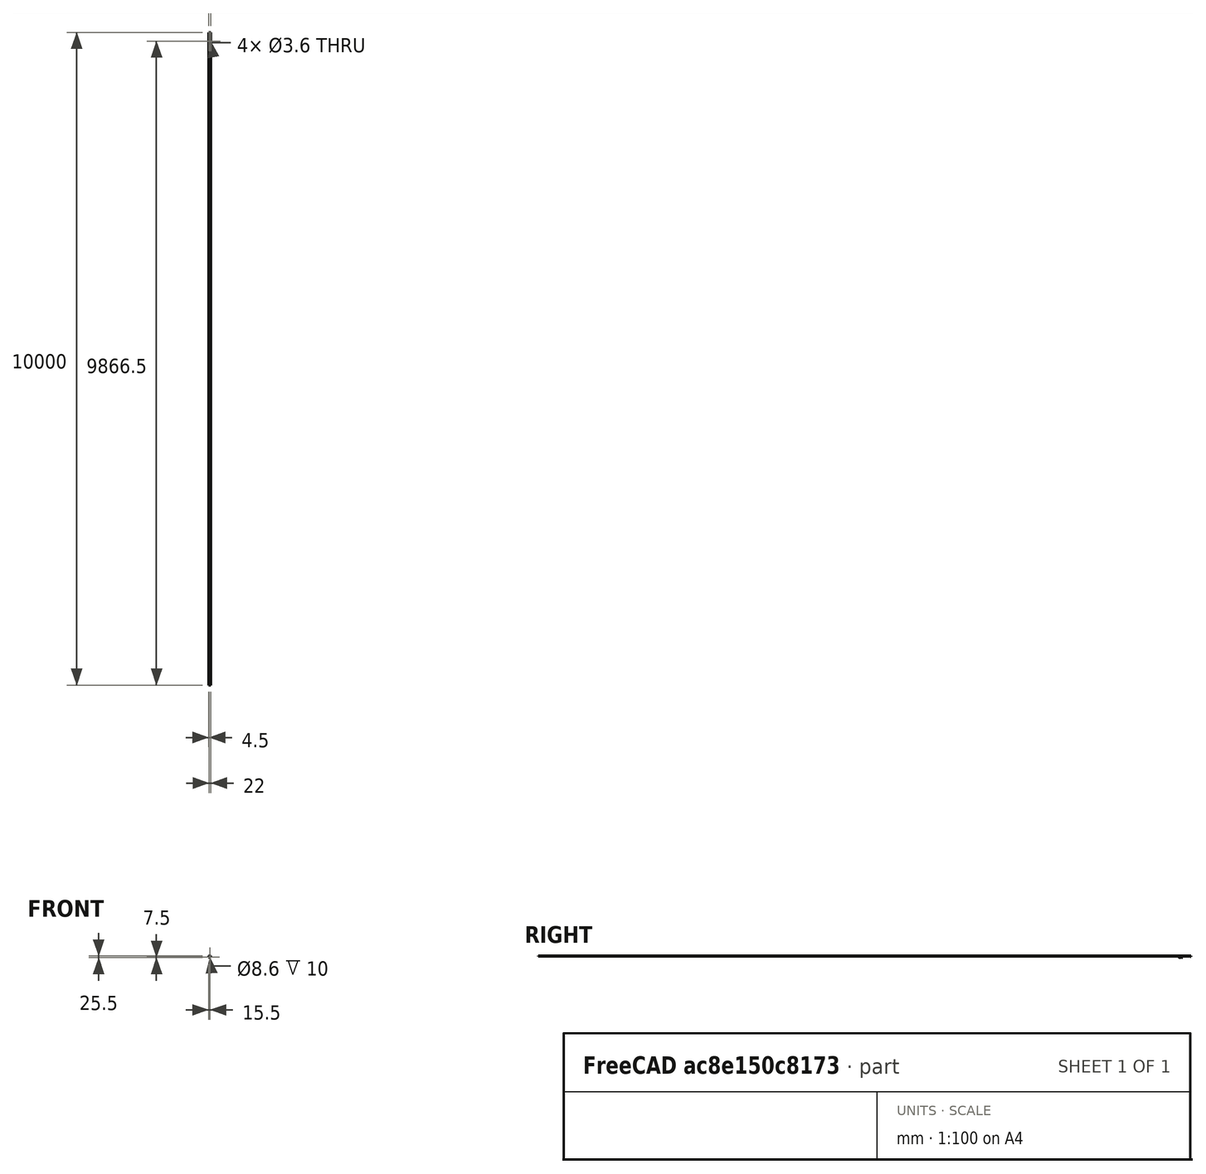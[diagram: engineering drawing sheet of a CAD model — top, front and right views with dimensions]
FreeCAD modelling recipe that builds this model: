
FCSTD DOCUMENT  (FreeCAD 0.15R4671 (Git))
Label: TopRodHolder
License: All rights reserved
LicenseURL: http://en.wikipedia.org/wiki/All_rights_reserved
objects: Sketcher::SketchObject×4, Mesh::Feature×3, PartDesign::Pocket×3, PartDesign::Fillet×2, Part::Feature×1, PartDesign::Pad×1
note: 15 computed .brp shape members not serialized (recipe doc carries the construction recipe); baked Part::Feature solids carry a one-line shape summary decoded from their .brp

FEATURE [Sketcher::SketchObject] Sketch
  Placement = pos=(0,0,0) rot=(1,0,0;3.14159rad)
  sketch-geometry (6):
    g0: LineSegment StartX=51 StartY=69.5 StartZ=0 EndX=21 EndY=69.5 EndZ=0
    g1: LineSegment StartX=21 StartY=69.5 StartZ=0 EndX=21 EndY=58.5 EndZ=0
    g2: LineSegment StartX=21 StartY=58.5 StartZ=0 EndX=51 EndY=58.5 EndZ=0
    g3: LineSegment StartX=51 StartY=58.5 StartZ=0 EndX=51 EndY=69.5 EndZ=0
    g4: Circle CenterX=47 CenterY=64 CenterZ=0 NormalX=0 NormalY=0 NormalZ=1 Radius=1.8
    g5: Circle CenterX=25 CenterY=64 CenterZ=0 NormalX=0 NormalY=0 NormalZ=1 Radius=1.8
  constraints (18):
    c: Coincident(g0,g1)
    c: Coincident(g1,g2)
    c: Coincident(g2,g3)
    c: Coincident(g3,g0)
    c: Horizontal(g0)
    c: Horizontal(g2)
    c: Vertical(g1)
    c: Vertical(g3)
    c: DistanceY(g0,g1) = -11
    c: DistanceX(g0,g0) = 30
    c: DistanceX(g1) = 21
    c: DistanceY(g1) = 58.5
    c: Radius(g4) = 1.8
    c: Radius(g5) = 1.8
    c: DistanceX(g5,g4) = 22
    c: DistanceY(g5,g4) = 0
    c: DistanceX(g5,g1) = -4
    c: DistanceY(g5,g1) = -5.5
FEATURE [Part::Feature] LM8UU_8mm_Linear_Bearing
  Placement = pos=(36,-114.5,-5.5) rot=(0,0,1;1.5708rad)
  shape: bbox 15 x 24 x 15 mm, 34 faces (baked)
FEATURE [Mesh::Feature] _mmRod_x100mm  label="8mmRod_x100mm"
  Placement = pos=(36,-160.5,-5.5) rot=(0,0,1;3.14159rad)
FEATURE [PartDesign::Pad] Pad
  Length = 11.5
  Length2 = 100
  Placement = pos=(0,0,0) rot=(1,0,0;3.14159rad)
  Sketch = -> Sketch
  Type = 0
FEATURE [Sketcher::SketchObject] Sketch001
  Placement = pos=(0,-69.5,0) rot=(0,0.707107,-0.707107;3.14159rad)
  Support = -> Pad [Face1]
  sketch-geometry (6):
    g0: ArcOfCircle CenterX=-36 CenterY=5.5 CenterZ=0 NormalX=0 NormalY=0 NormalZ=1 Radius=6 StartAngle=0 EndAngle=3.14159
    g1: LineSegment StartX=-30 StartY=5.5 StartZ=0 EndX=-20.5 EndY=5.5 EndZ=0
    g2: LineSegment StartX=-20.5 StartY=5.5 StartZ=0 EndX=-20.5 EndY=12.5 EndZ=0
    g3: LineSegment StartX=-20.5 StartY=12.5 StartZ=0 EndX=-51.5 EndY=12.5 EndZ=0
    g4: LineSegment StartX=-51.5 StartY=12.5 StartZ=0 EndX=-51.5 EndY=5.5 EndZ=0
    g5: LineSegment StartX=-51.5 StartY=5.5 StartZ=0 EndX=-42 EndY=5.5 EndZ=0
  constraints (6):
    c: Coincident(g1,g2)
    c: Coincident(g2,g3)
    c: Coincident(g3,g4)
    c: Coincident(g4,g5)
    c: Coincident(g0,g5)
    c: Coincident(g0,g1)
FEATURE [PartDesign::Pocket] Pocket
  Length = 5
  Placement = pos=(0,0,0) rot=(1,0,0;3.14159rad)
  Sketch = -> Sketch001
  Type = 1
FEATURE [Mesh::Feature] HexNutStyle1_M  label="HexNutStyle1_M3"
  Placement = pos=(39.2,-42,-122) rot=(0,0,1;0rad)
FEATURE [Mesh::Feature] HexNutStyle1_M001  label="HexNutStyle1_M004"
  Placement = pos=(61.2,-42,-122) rot=(0,0,1;0rad)
FEATURE [Sketcher::SketchObject] Sketch002
  Placement = pos=(0,0,-5.5) rot=(1,0,0;3.14159rad)
  Support = -> Pocket [Face4]
  sketch-geometry (14):
    g0: LineSegment StartX=25 StartY=67.5 StartZ=0 EndX=21.9689 EndY=65.75 EndZ=0
    g1: LineSegment StartX=21.9689 StartY=65.75 StartZ=0 EndX=21.9689 EndY=62.25 EndZ=0
    g2: LineSegment StartX=21.9689 StartY=62.25 StartZ=0 EndX=25 EndY=60.5 EndZ=0
    g3: LineSegment StartX=25 StartY=60.5 StartZ=0 EndX=28.0311 EndY=62.25 EndZ=0
    g4: LineSegment StartX=28.0311 StartY=62.25 StartZ=0 EndX=28.0311 EndY=65.75 EndZ=0
    g5: LineSegment StartX=28.0311 StartY=65.75 StartZ=0 EndX=25 EndY=67.5 EndZ=0
    g6: Circle [constr] CenterX=25 CenterY=64 CenterZ=0 NormalX=0 NormalY=0 NormalZ=1 Radius=3.5
    g7: LineSegment StartX=47 StartY=67.5 StartZ=0 EndX=43.9689 EndY=65.75 EndZ=0
    g8: LineSegment StartX=43.9689 StartY=65.75 StartZ=0 EndX=43.9689 EndY=62.25 EndZ=0
    g9: LineSegment StartX=43.9689 StartY=62.25 StartZ=0 EndX=47 EndY=60.5 EndZ=0
    g10: LineSegment StartX=47 StartY=60.5 StartZ=0 EndX=50.0311 EndY=62.25 EndZ=0
    g11: LineSegment StartX=50.0311 StartY=62.25 StartZ=0 EndX=50.0311 EndY=65.75 EndZ=0
    g12: LineSegment StartX=50.0311 StartY=65.75 StartZ=0 EndX=47 EndY=67.5 EndZ=0
    g13: Circle [constr] CenterX=47 CenterY=64 CenterZ=0 NormalX=0 NormalY=0 NormalZ=1 Radius=3.5
  constraints (26):
    c: Coincident(g0,g1)
    c: Coincident(g1,g2)
    c: Coincident(g2,g3)
    c: Coincident(g3,g4)
    c: Coincident(g4,g5)
    c: Coincident(g5,g0)
    c: Equal(g0, g1-g5) x5
    c: PointOnObject(g0,g6)
    c: PointOnObject(g1,g6)
    c: PointOnObject(g2,g6)
    c: PointOnObject(g3,g6)
    c: PointOnObject(g4,g6)
    c: PointOnObject(g5,g6)
    c: Coincident(g7,g8)
    c: Coincident(g8,g9)
    c: Coincident(g9,g10)
    c: Coincident(g10,g11)
    c: Coincident(g11,g12)
    c: Coincident(g12,g7)
    c: Equal(g7, g8-g12) x5
    c: PointOnObject(g7,g13)
    c: PointOnObject(g8,g13)
    c: PointOnObject(g9,g13)
    c: PointOnObject(g10,g13)
    c: PointOnObject(g11,g13)
    c: PointOnObject(g12,g13)
FEATURE [PartDesign::Pocket] Pocket001
  Length = 4
  Placement = pos=(0,0,0) rot=(1,0,0;3.14159rad)
  Sketch = -> Sketch002
  Type = 0
FEATURE [Sketcher::SketchObject] Sketch003
  Placement = pos=(0,-69.5,0) rot=(0,0.707107,-0.707107;3.14159rad)
  Support = -> Pocket001 [Face1]
  sketch-geometry (1):
    g0: Circle CenterX=-36 CenterY=5.5 CenterZ=0 NormalX=0 NormalY=0 NormalZ=1 Radius=4.3
  constraints (1):
    c: Radius(g0) = 4.3
FEATURE [PartDesign::Pocket] Pocket002
  Length = 10
  Placement = pos=(0,0,0) rot=(1,0,0;3.14159rad)
  Sketch = -> Sketch003
  Type = 0
FEATURE [PartDesign::Fillet] Fillet
  Base = -> Pocket002 [Edge18,Edge26]
  Placement = pos=(0,0,0) rot=(1,0,0;3.14159rad)
  Radius = 2
FEATURE [PartDesign::Fillet] Fillet001  label="TopRodHolder"
  Base = -> Fillet [Edge7,Edge32,Edge3,Edge23]
  Placement = pos=(0,0,0) rot=(1,0,0;3.14159rad)
  Radius = 2
